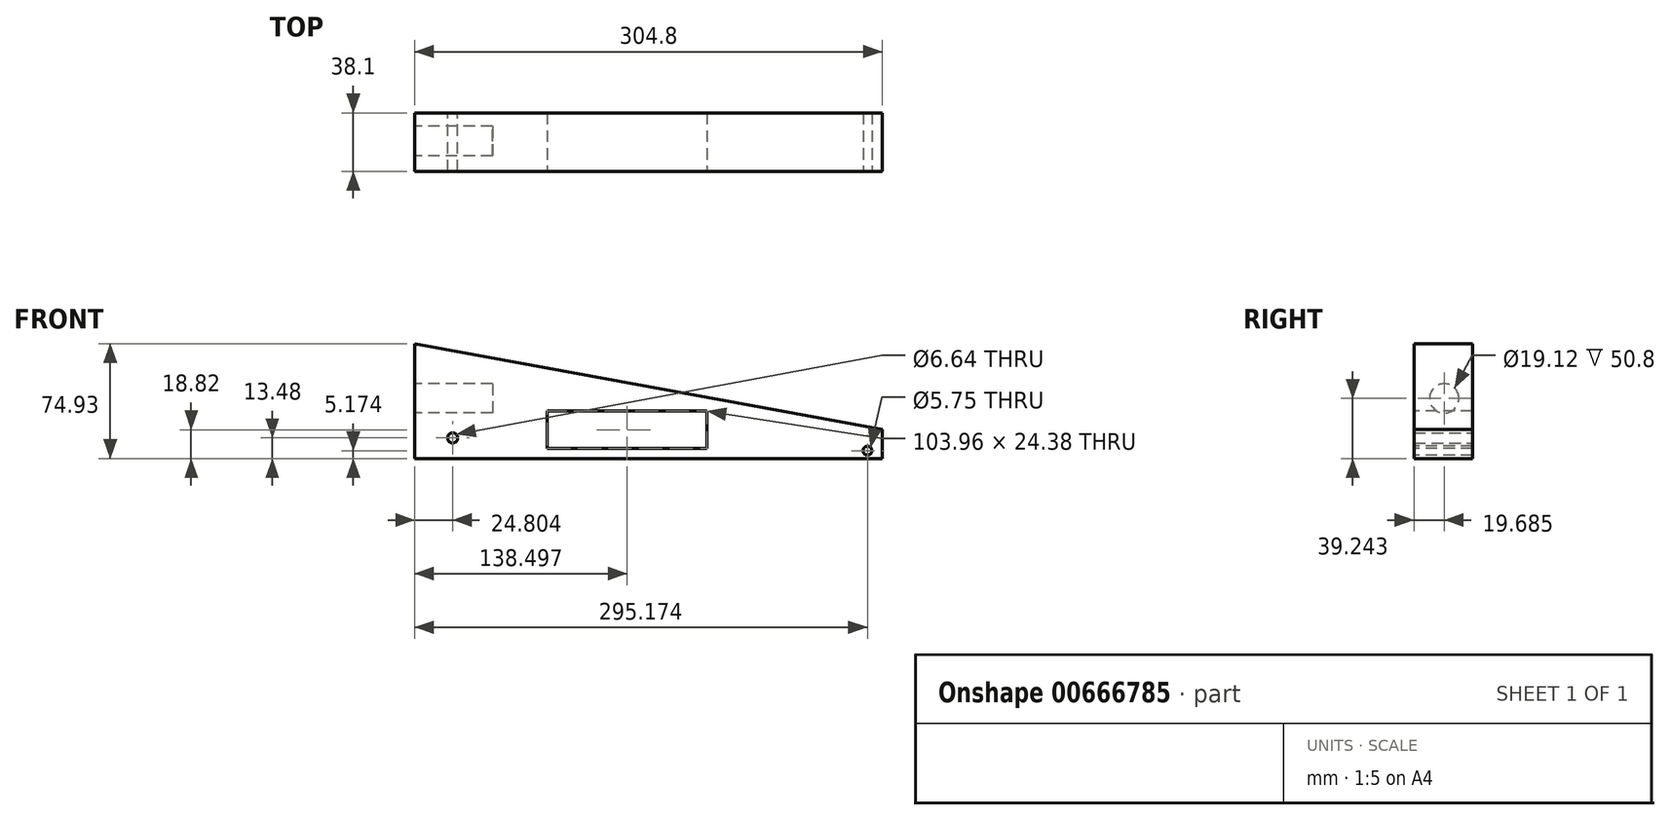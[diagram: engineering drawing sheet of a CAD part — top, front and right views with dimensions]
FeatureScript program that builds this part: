
annotation { "Feature Type Name" : "Feature", "Feature Type Description" : "" }
export const myFeature = defineFeature(function(context is Context, id is Id, definition is map)
    precondition{}
    {
        {
            var Q0;
            Q0=qCreatedBy(makeId("Front.planeOp"),FACE);
            var sketch = newSketch(context, id + "F0", { "sketchPlane" : qUnion([Q0])});
            skLineSegment(sketch, "E0", {"start": v(0, 0) * mm, "end": v(0, 74.93) * mm});
            skLineSegment(sketch, "E1", {"start": v(304.8, 0) * mm, "end": v(0, 0) * mm});
            skLineSegment(sketch, "E2", {"start": v(0, 74.93) * mm, "end": v(304.8, 19.05) * mm});
            skLineSegment(sketch, "E3", {"start": v(304.8, 19.05) * mm, "end": v(304.8, 0) * mm});
            skSolve(sketch);
        }
        {
            var Q0;
            Q0 = qSketchRegion(id + "F0", true);
            extrude(context, id + "F1", {"entities" : qUnion([Q0]), "depth" : 38.1 * mm, "offsetDistance" : 25.4 * mm});
        }
        {
            var Q0;
            Q0=makeQuery(id+"F1.opExtrude","SWEPT_FACE",FACE,{"disambiguationData":[OSD([sQuery(id+"F0.wireOp",EDGE,"E0")])]});
            var sketch = newSketch(context, id + "F2", { "sketchPlane" : qUnion([Q0])});
            skCircle(sketch, "E4", {"center": v(18.42, 39.24) * mm, "radius": 9.56 * mm});
            skSolve(sketch);
        }
        {
            var Q0;
            Q0=makeQuery(id+"F2.imprint","IMPRINT",FACE,{"disambiguationData":[TD([[makeQuery(id+"F2.imprint","IMPRINT",EDGE,{"derivedFrom":sQuery(id+"F2.wireOp",EDGE,"E4")}),1.0]])]});
            extrude(context, id + "F3", {"entities" : qUnion([Q0]), "operationType" : NewBodyOperationType.REMOVE, "oppositeDirection" : true, "depth" : 50.8 * mm, "offsetDistance" : 25.4 * mm});
        }
        {
            var Q0;
            Q0=makeQuery(id+"F1.opExtrude","CAP_FACE",FACE,{"disambiguationData":[OSD([sQuery(id+"F0.wireOp",EDGE,"E0"),sQuery(id+"F0.wireOp",EDGE,"E1"),sQuery(id+"F0.wireOp",EDGE,"E2"),sQuery(id+"F0.wireOp",EDGE,"E3")])],"isStart":true});
            var sketch = newSketch(context, id + "F4", { "sketchPlane" : qUnion([Q0])});
            skCircle(sketch, "E5", {"center": v(-24.8, 13.48) * mm, "radius": 3.32 * mm});
            skSolve(sketch);
        }
        {
            var Q0;
            Q0=makeQuery(id+"F4.imprint","IMPRINT",FACE,{"disambiguationData":[TD([[makeQuery(id+"F4.imprint","IMPRINT",EDGE,{"derivedFrom":sQuery(id+"F4.wireOp",EDGE,"E5")}),1.0]])]});
            extrude(context, id + "F5", {"entities" : qUnion([Q0]), "operationType" : NewBodyOperationType.REMOVE, "oppositeDirection" : true, "depth" : 42.93 * mm, "offsetDistance" : 25.4 * mm});
        }
        {
            var Q0;
            Q0=makeQuery(id+"F1.opExtrude","CAP_FACE",FACE,{"disambiguationData":[OSD([sQuery(id+"F0.wireOp",EDGE,"E0"),sQuery(id+"F0.wireOp",EDGE,"E1"),sQuery(id+"F0.wireOp",EDGE,"E2"),sQuery(id+"F0.wireOp",EDGE,"E3")])],"isStart":false});
            var sketch = newSketch(context, id + "F6", { "sketchPlane" : qUnion([Q0])});
            skLineSegment(sketch, "E6.bottom", {"start": v(86.52, 31) * mm, "end": v(190.47, 31) * mm});
            skLineSegment(sketch, "E6.top", {"start": v(86.52, 6.63) * mm, "end": v(190.47, 6.63) * mm});
            skLineSegment(sketch, "E6.left", {"start": v(86.52, 31) * mm, "end": v(86.52, 6.63) * mm});
            skLineSegment(sketch, "E6.right", {"start": v(190.47, 31) * mm, "end": v(190.47, 6.63) * mm});
            skSolve(sketch);
        }
        {
            var Q0;
            Q0=makeQuery(id+"F6.imprint","IMPRINT",FACE,{"disambiguationData":[TD([[makeQuery(id+"F6.imprint","IMPRINT",EDGE,{"derivedFrom":sQuery(id+"F6.wireOp",EDGE,"E6.bottom")}),-1.0]])]});
            extrude(context, id + "F7", {"entities" : qUnion([Q0]), "operationType" : NewBodyOperationType.REMOVE, "oppositeDirection" : true, "depth" : 50.8 * mm, "offsetDistance" : 25.4 * mm});
        }
        {
            var Q0;
            Q0=makeQuery(id+"F1.opExtrude","CAP_FACE",FACE,{"disambiguationData":[OSD([sQuery(id+"F0.wireOp",EDGE,"E0"),sQuery(id+"F0.wireOp",EDGE,"E1"),sQuery(id+"F0.wireOp",EDGE,"E2"),sQuery(id+"F0.wireOp",EDGE,"E3")])],"isStart":false});
            var sketch = newSketch(context, id + "F8", { "sketchPlane" : qUnion([Q0])});
            skCircle(sketch, "E7", {"center": v(295.17, 5.17) * mm, "radius": 2.88 * mm});
            skSolve(sketch);
        }
        {
            var Q0;
            Q0=makeQuery(id+"F8.imprint","IMPRINT",FACE,{"disambiguationData":[TD([[makeQuery(id+"F8.imprint","IMPRINT",EDGE,{"derivedFrom":sQuery(id+"F8.wireOp",EDGE,"E7")}),1.0]])]});
            extrude(context, id + "F9", {"entities" : qUnion([Q0]), "operationType" : NewBodyOperationType.REMOVE, "oppositeDirection" : true, "depth" : 45.2 * mm, "offsetDistance" : 25.4 * mm});
        }
    });
